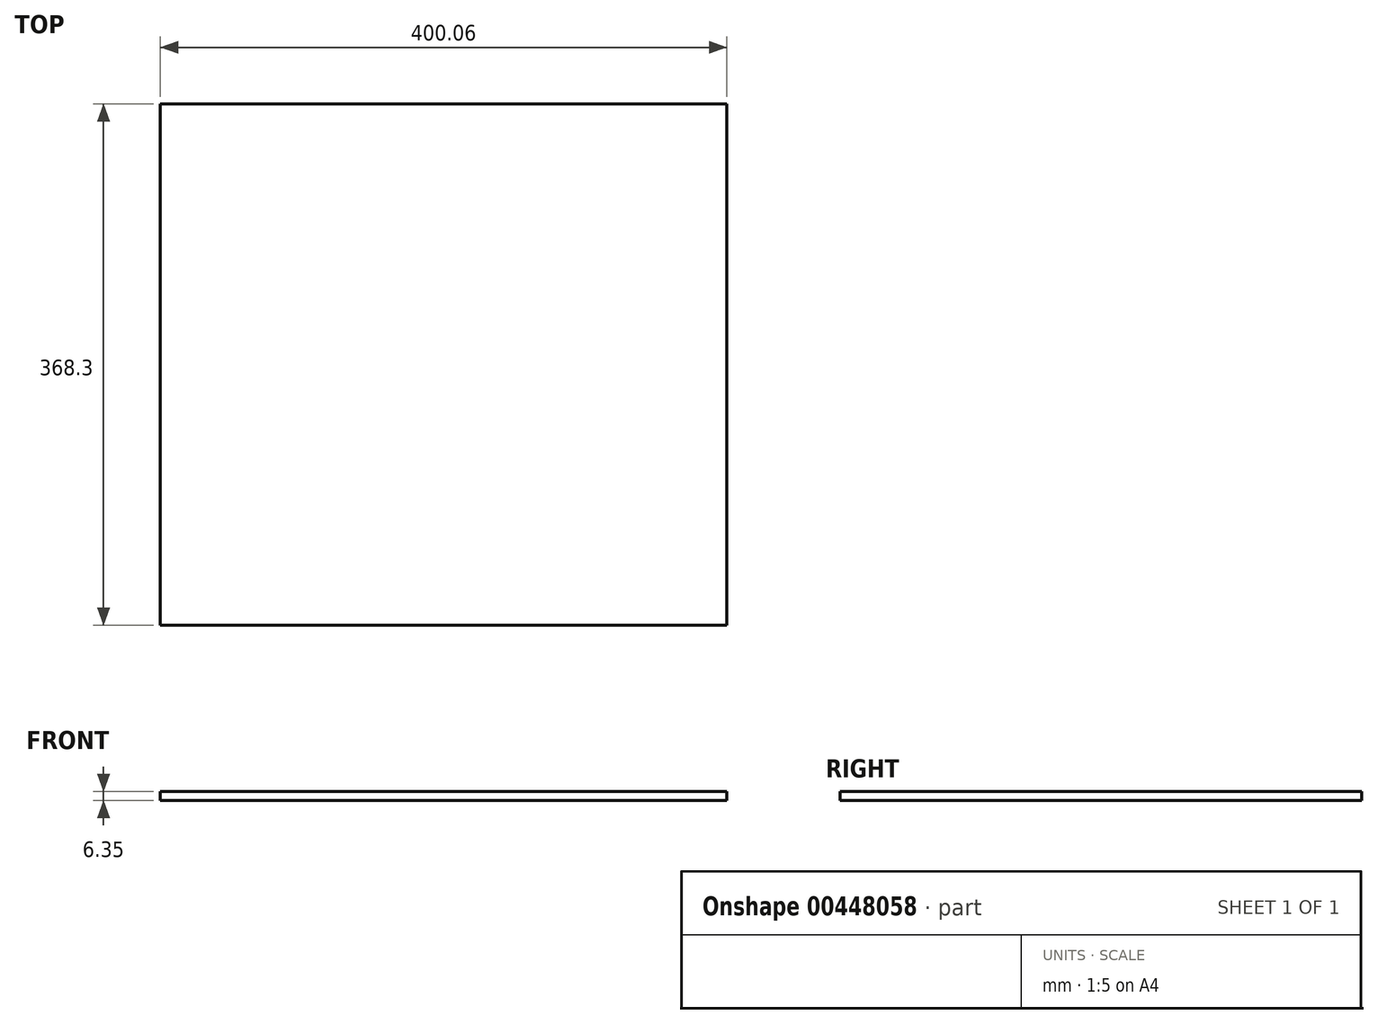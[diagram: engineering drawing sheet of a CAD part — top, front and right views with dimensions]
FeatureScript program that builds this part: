
annotation { "Feature Type Name" : "Feature", "Feature Type Description" : "" }
export const myFeature = defineFeature(function(context is Context, id is Id, definition is map)
    precondition{}
    {
        {
            var Q0;
            Q0=qCreatedBy(makeId("Top.planeOp"),FACE);
            var sketch = newSketch(context, id + "F0", { "sketchPlane" : qUnion([Q0])});
            skLineSegment(sketch, "E0.bottom", {"start": v(-200.02, 184.15) * mm, "end": v(200.03, 184.15) * mm});
            skLineSegment(sketch, "E0.top", {"start": v(-200.03, -184.15) * mm, "end": v(200.03, -184.15) * mm});
            skLineSegment(sketch, "E0.left", {"start": v(-200.02, 184.15) * mm, "end": v(-200.03, -184.15) * mm});
            skLineSegment(sketch, "E0.right", {"start": v(200.03, 184.15) * mm, "end": v(200.03, -184.15) * mm});
            skPoint(sketch, "E0.middle", {"position": v(0, 0) * mm});
            skSolve(sketch);
        }
        {
            var Q0;
            Q0 = qSketchRegion(id + "F0", true);
            extrude(context, id + "F1", {"entities" : qUnion([Q0]), "depth" : 6.35 * mm});
        }
    });
